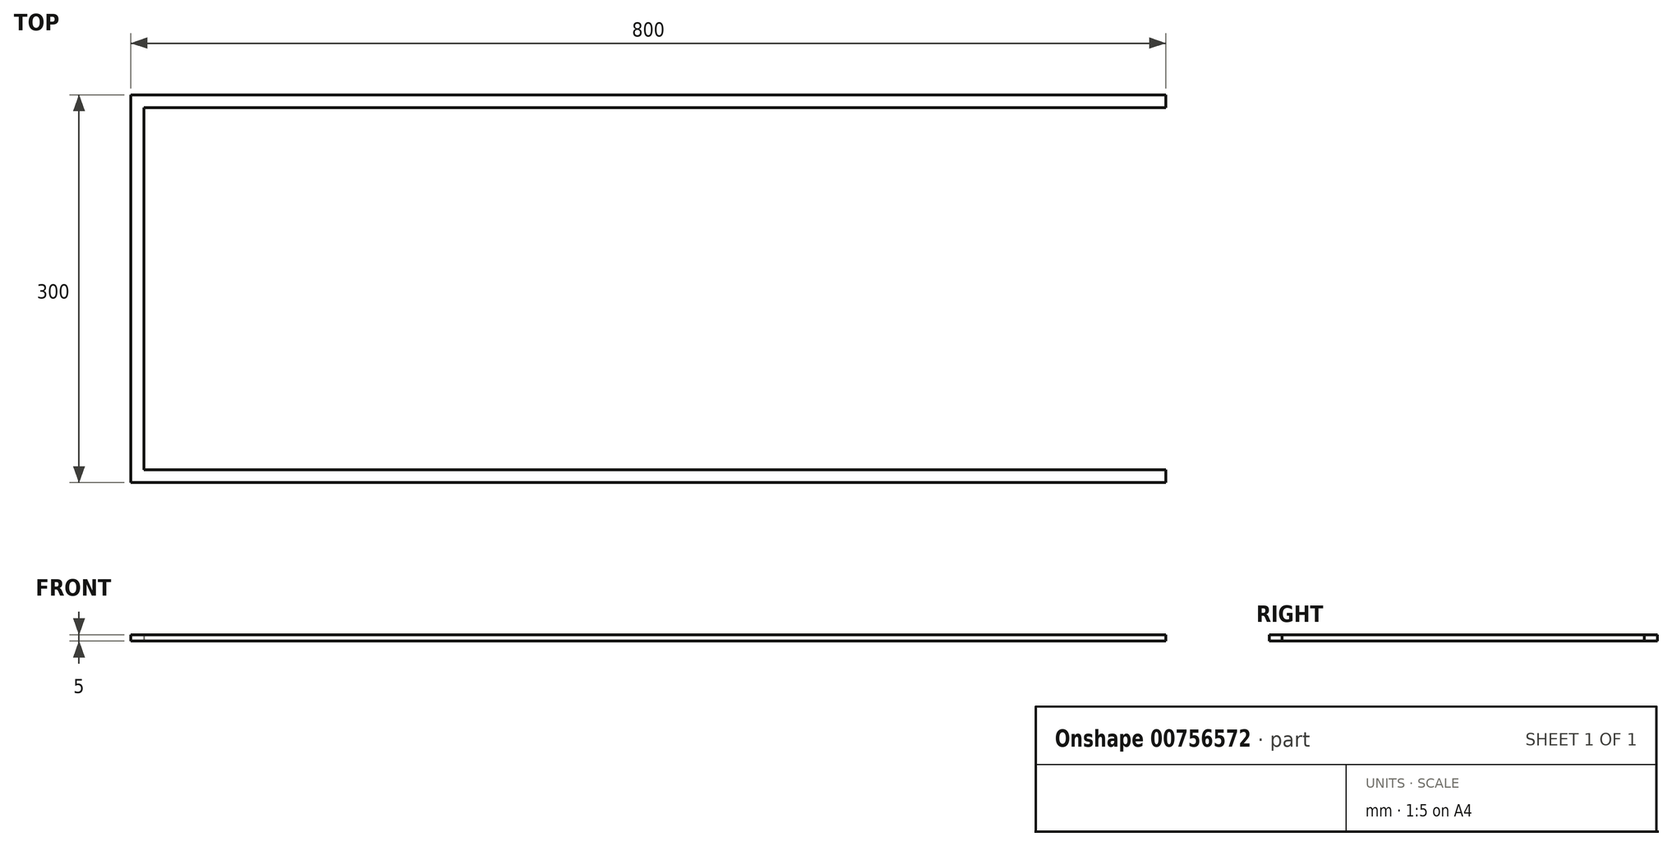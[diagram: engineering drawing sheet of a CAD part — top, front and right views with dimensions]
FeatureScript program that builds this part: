
annotation { "Feature Type Name" : "Feature", "Feature Type Description" : "" }
export const myFeature = defineFeature(function(context is Context, id is Id, definition is map)
    precondition{}
    {
        {
            var Q0;
            Q0=qCreatedBy(makeId("Top.planeOp"),FACE);
            var sketch = newSketch(context, id + "F0", { "sketchPlane" : qUnion([Q0])});
            skLineSegment(sketch, "E0.bottom", {"start": v(0, 0) * mm, "end": v(10, 0) * mm});
            skLineSegment(sketch, "E0.top", {"start": v(0, 300) * mm, "end": v(10, 300) * mm});
            skLineSegment(sketch, "E0.left", {"start": v(0, 0) * mm, "end": v(0, 300) * mm});
            skLineSegment(sketch, "E0.right", {"start": v(10, 10) * mm, "end": v(10, 290) * mm});
            skLineSegment(sketch, "E1.bottom", {"start": v(0, 0) * mm, "end": v(800, 0) * mm});
            skLineSegment(sketch, "E1.top", {"start": v(10, 10) * mm, "end": v(800, 10) * mm});
            skLineSegment(sketch, "E1.left", {"start": v(0, 0) * mm, "end": v(0, 10) * mm});
            skLineSegment(sketch, "E1.right", {"start": v(800, 0) * mm, "end": v(800, 10) * mm});
            skLineSegment(sketch, "E2.bottom", {"start": v(0, 300) * mm, "end": v(800, 300) * mm});
            skLineSegment(sketch, "E2.top", {"start": v(10, 290) * mm, "end": v(800, 290) * mm});
            skLineSegment(sketch, "E2.left", {"start": v(0, 300) * mm, "end": v(0, 290) * mm});
            skLineSegment(sketch, "E2.right", {"start": v(800, 300) * mm, "end": v(800, 290) * mm});
            skSolve(sketch);
        }
        {
            var Q0;
            Q0=makeQuery(id+"F0.imprint","IMPRINT",FACE,{"disambiguationData":[TD([[makeQuery(id+"F0.imprint","IMPRINT",EDGE,{"derivedFrom":sQuery(id+"F0.wireOp",EDGE,"E0.left")}),-1.0]])]});
            extrude(context, id + "F1", {"entities" : qUnion([Q0]), "depth" : 5 * mm, "offsetDistance" : 25 * mm});
        }
    });
